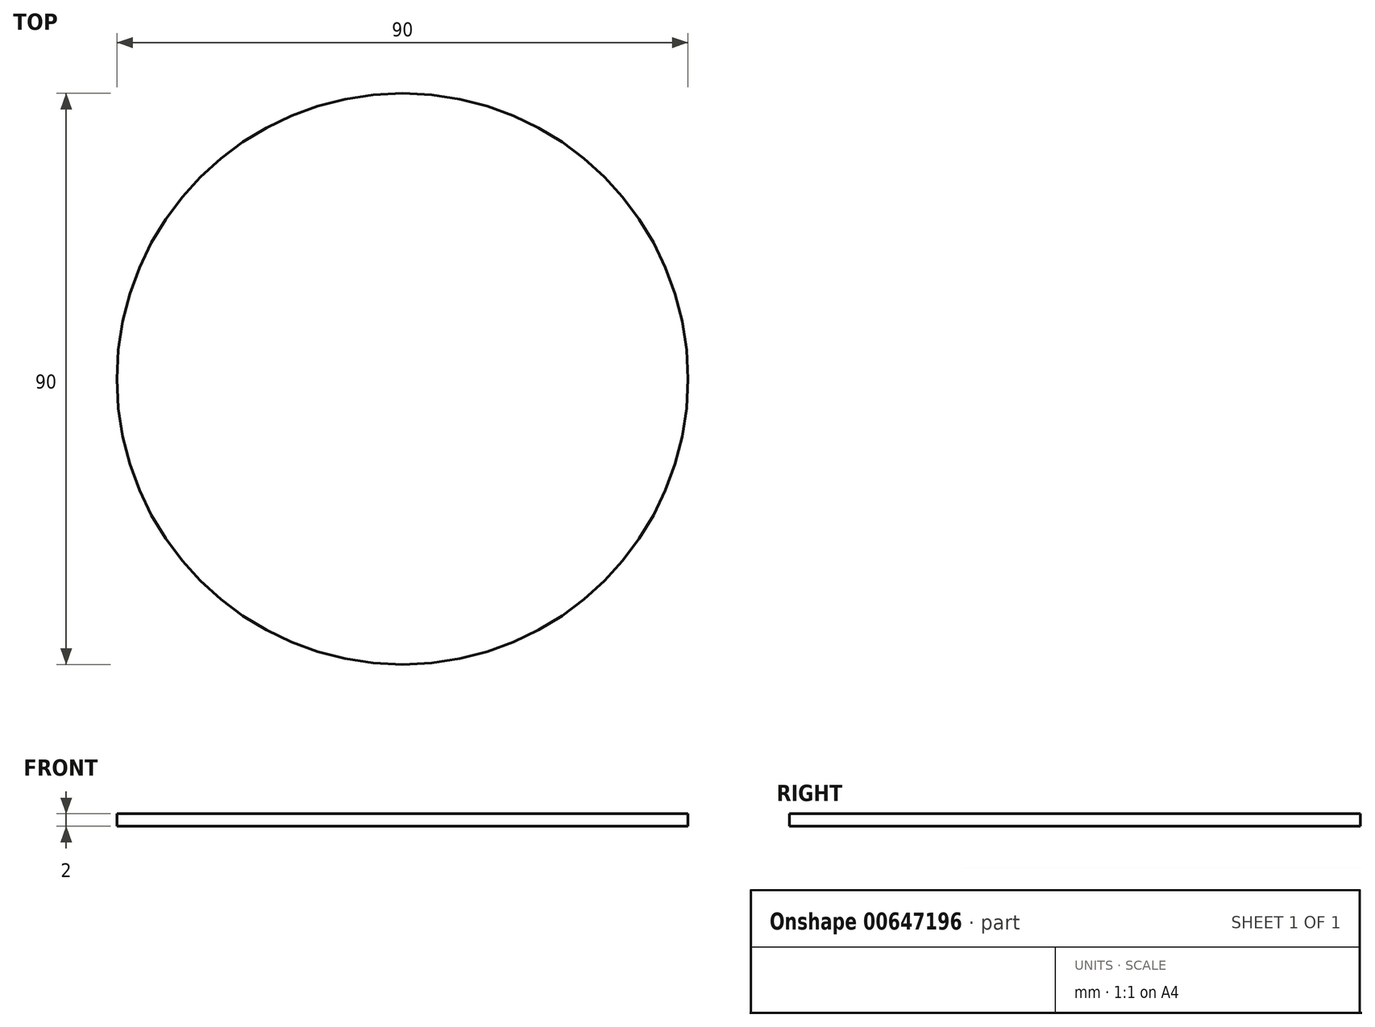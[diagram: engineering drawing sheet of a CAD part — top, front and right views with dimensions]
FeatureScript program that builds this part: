
annotation { "Feature Type Name" : "Feature", "Feature Type Description" : "" }
export const myFeature = defineFeature(function(context is Context, id is Id, definition is map)
    precondition{}
    {
        {
            var Q0;
            Q0=qCreatedBy(makeId("Top.planeOp"),FACE);
            var sketch = newSketch(context, id + "F0", { "sketchPlane" : qUnion([Q0])});
            skCircle(sketch, "E0", {"center": v(0, 0) * mm, "radius": 45 * mm});
            skSolve(sketch);
        }
        {
            var Q0;
            Q0=makeQuery(id+"F0.imprint","IMPRINT",FACE,{"disambiguationData":[TD([[makeQuery(id+"F0.imprint","IMPRINT",EDGE,{"derivedFrom":sQuery(id+"F0.wireOp",EDGE,"E0")}),1.0]])]});
            extrude(context, id + "F1", {"entities" : qUnion([Q0]), "depth" : 2 * mm, "offsetDistance" : 25 * mm});
        }
    });
